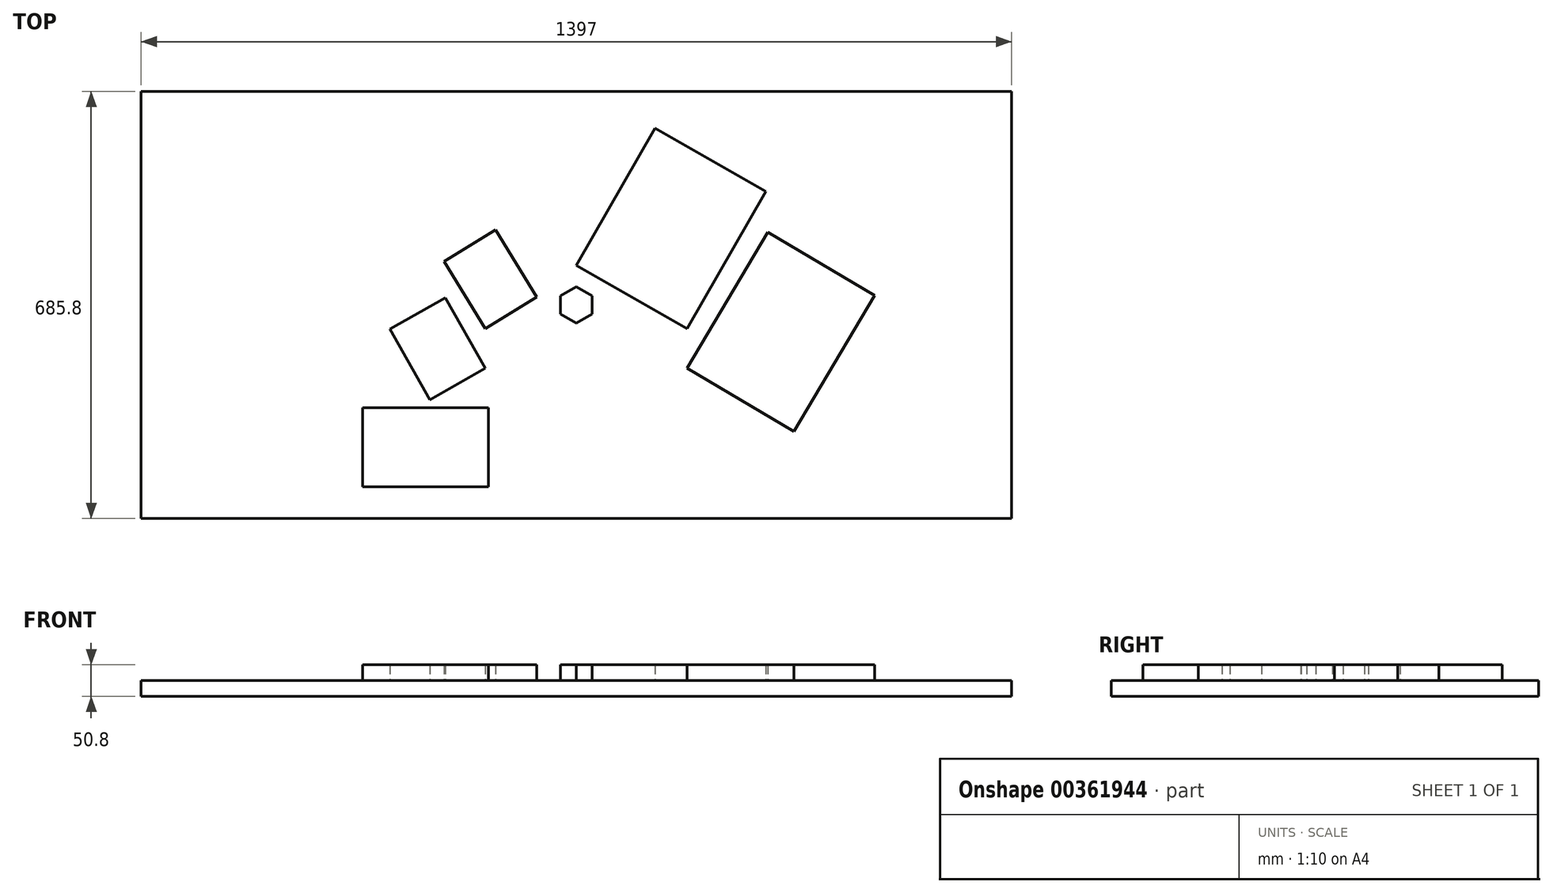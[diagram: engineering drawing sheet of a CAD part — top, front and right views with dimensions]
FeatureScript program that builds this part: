
annotation { "Feature Type Name" : "Feature", "Feature Type Description" : "" }
export const myFeature = defineFeature(function(context is Context, id is Id, definition is map)
    precondition{}
    {
        {
            var Q0;
            Q0=qCreatedBy(makeId("Top.planeOp"),FACE);
            var sketch = newSketch(context, id + "F0", { "sketchPlane" : qUnion([Q0])});
            skLineSegment(sketch, "E0.bottom", {"start": v(698.5, 342.9) * mm, "end": v(-698.5, 342.9) * mm});
            skLineSegment(sketch, "E0.top", {"start": v(698.5, -342.9) * mm, "end": v(-698.5, -342.9) * mm});
            skLineSegment(sketch, "E0.left", {"start": v(698.5, 342.9) * mm, "end": v(698.5, -342.9) * mm});
            skLineSegment(sketch, "E0.right", {"start": v(-698.5, 342.9) * mm, "end": v(-698.5, -342.9) * mm});
            skPoint(sketch, "E0.middle", {"position": v(0, 0) * mm});
            skSolve(sketch);
        }
        {
            var Q0;
            Q0=qSketchRegion(id+"F0",true);
            extrude(context, id + "F1", {"entities" : qUnion([Q0]), "depth" : 25.4 * mm});
        }
        {
            var Q0;
            Q0=makeQuery(id+"F1.opExtrude","CAP_FACE",FACE,{"disambiguationData":[OSD([sQuery(id+"F0.wireOp",EDGE,"E0.bottom"),sQuery(id+"F0.wireOp",EDGE,"E0.top"),sQuery(id+"F0.wireOp",EDGE,"E0.left"),sQuery(id+"F0.wireOp",EDGE,"E0.right")])],"isStart":false});
            var sketch = newSketch(context, id + "F2", { "sketchPlane" : qUnion([Q0])});
            skLineSegment(sketch, "E1.bottom", {"start": v(-120.65, -152.4) * mm, "end": v(120.65, -152.4) * mm, "construction": true});
            skLineSegment(sketch, "E1.top", {"start": v(-120.65, -50.8) * mm, "end": v(120.65, -50.8) * mm, "construction": true});
            skLineSegment(sketch, "E1.left", {"start": v(-120.65, -152.4) * mm, "end": v(-120.65, -50.8) * mm, "construction": true});
            skLineSegment(sketch, "E1.right", {"start": v(120.65, -152.4) * mm, "end": v(120.65, -50.8) * mm, "construction": true});
            skCircle(sketch, "E2.cCircle", {"center": v(0, 0) * mm, "radius": 25.4 * mm, "construction": true});
            skLineSegment(sketch, "E2.0", {"start": v(25.4, 14.66) * mm, "end": v(25.4, -14.66) * mm});
            skLineSegment(sketch, "E2.1", {"start": v(25.4, -14.66) * mm, "end": v(0, -29.33) * mm});
            skLineSegment(sketch, "E2.2", {"start": v(0, -29.33) * mm, "end": v(-25.4, -14.66) * mm});
            skLineSegment(sketch, "E2.3", {"start": v(-25.4, -14.66) * mm, "end": v(-25.4, 14.66) * mm});
            skLineSegment(sketch, "E2.4", {"start": v(-25.4, 14.66) * mm, "end": v(0, 29.33) * mm});
            skLineSegment(sketch, "E2.5", {"start": v(0, 29.33) * mm, "end": v(25.4, 14.66) * mm});
            skPoint(sketch, "E2.0.midPoint", {"position": v(25.4, 0) * mm});
            skPoint(sketch, "E3.endSnap0", {"position": v(0, 342.9) * mm});
            skPoint(sketch, "E4", {"position": v(0, -50.8) * mm});
            skLineSegment(sketch, "E5.bottom", {"start": v(177.8, -101.6) * mm, "end": v(349.25, -203.2) * mm});
            skLineSegment(sketch, "E5.top", {"start": v(307.29, 116.91) * mm, "end": v(478.74, 15.31) * mm});
            skLineSegment(sketch, "E5.left", {"start": v(177.8, -101.6) * mm, "end": v(307.29, 116.91) * mm});
            skLineSegment(sketch, "E5.right", {"start": v(349.25, -203.2) * mm, "end": v(478.74, 15.31) * mm});
            skPoint(sketch, "E6", {"position": v(263.52, -152.4) * mm});
            skPoint(sketch, "E7", {"position": v(120.65, -101.6) * mm});
            skLineSegment(sketch, "E8.bottom", {"start": v(0, 63.5) * mm, "end": v(177.8, -38.1) * mm});
            skLineSegment(sketch, "E8.top", {"start": v(126.02, 284.03) * mm, "end": v(303.82, 182.43) * mm});
            skLineSegment(sketch, "E8.left", {"start": v(0, 63.5) * mm, "end": v(126.02, 284.03) * mm});
            skLineSegment(sketch, "E8.right", {"start": v(177.8, -38.1) * mm, "end": v(303.82, 182.43) * mm});
            skPoint(sketch, "E9", {"position": v(88.9, 12.7) * mm});
            skLineSegment(sketch, "E10.bottom", {"start": v(-146.05, -38.1) * mm, "end": v(-63.5, 12.7) * mm});
            skLineSegment(sketch, "E10.top", {"start": v(-212.48, 69.85) * mm, "end": v(-129.93, 120.65) * mm});
            skLineSegment(sketch, "E10.left", {"start": v(-146.05, -38.1) * mm, "end": v(-212.48, 69.85) * mm});
            skLineSegment(sketch, "E10.right", {"start": v(-63.5, 12.7) * mm, "end": v(-129.93, 120.65) * mm});
            skPoint(sketch, "E11", {"position": v(-104.78, -12.7) * mm});
            skLineSegment(sketch, "E12.bottom", {"start": v(-234.95, -152.4) * mm, "end": v(-146.05, -101.8) * mm});
            skLineSegment(sketch, "E12.top", {"start": v(-299.5, -38.97) * mm, "end": v(-210.6, 11.62) * mm});
            skLineSegment(sketch, "E12.left", {"start": v(-234.95, -152.4) * mm, "end": v(-299.5, -38.97) * mm});
            skLineSegment(sketch, "E12.right", {"start": v(-146.05, -101.8) * mm, "end": v(-210.6, 11.62) * mm});
            skPoint(sketch, "E13", {"position": v(-190.5, -127.1) * mm});
            skLineSegment(sketch, "E14.bottom", {"start": v(-141.23, -292.1) * mm, "end": v(-141.23, -165.1) * mm});
            skLineSegment(sketch, "E14.top", {"start": v(-342.9, -292.1) * mm, "end": v(-342.9, -165.1) * mm});
            skLineSegment(sketch, "E14.left", {"start": v(-141.23, -292.1) * mm, "end": v(-342.9, -292.1) * mm});
            skLineSegment(sketch, "E14.right", {"start": v(-141.23, -165.1) * mm, "end": v(-342.9, -165.1) * mm});
            skPoint(sketch, "E15", {"position": v(-141.23, -228.6) * mm});
            skSolve(sketch);
        }
        {
            var Q0;
            Q0=qSketchRegion(id+"F2",true);
            extrude(context, id + "F3", {"entities" : qUnion([Q0]), "depth" : 25.4 * mm});
        }
    });
